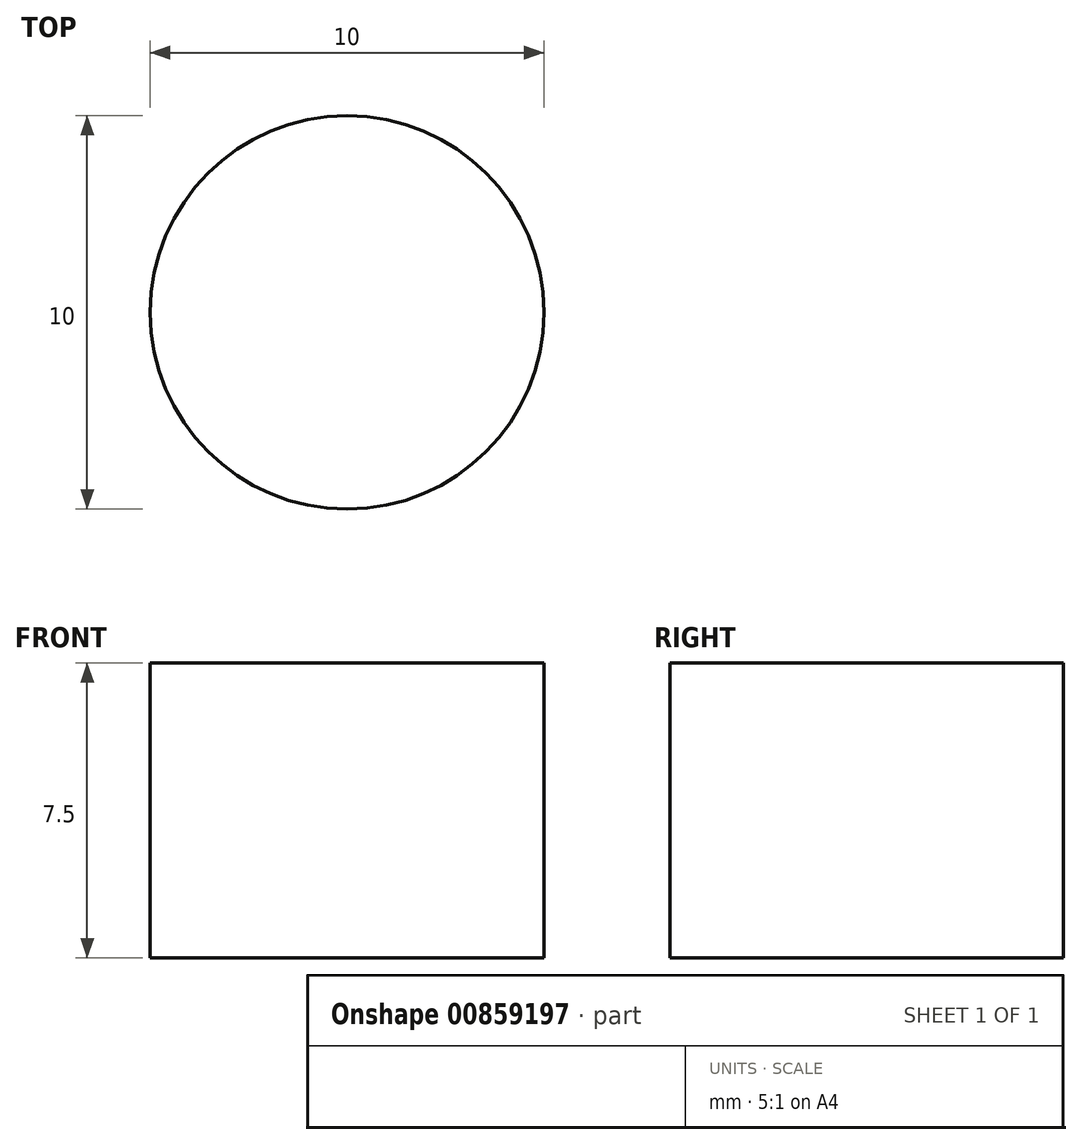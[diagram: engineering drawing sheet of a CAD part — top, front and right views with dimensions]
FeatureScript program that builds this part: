
annotation { "Feature Type Name" : "Feature", "Feature Type Description" : "" }
export const myFeature = defineFeature(function(context is Context, id is Id, definition is map)
    precondition{}
    {
        {
            var Q0;
            Q0=qCreatedBy(makeId("Top.planeOp"),FACE);
            var sketch = newSketch(context, id + "F0", { "sketchPlane" : qUnion([Q0])});
            skCircle(sketch, "E0", {"center": v(0, 0) * mm, "radius": 5 * mm});
            skSolve(sketch);
        }
        {
            var Q0;
            Q0 = qSketchRegion(id + "F0", true);
            extrude(context, id + "F1", {"entities" : qUnion([Q0]), "endBound" : BoundingType.SYMMETRIC, "depth" : 7.5 * mm, "offsetDistance" : 25.4 * mm});
        }
    });
